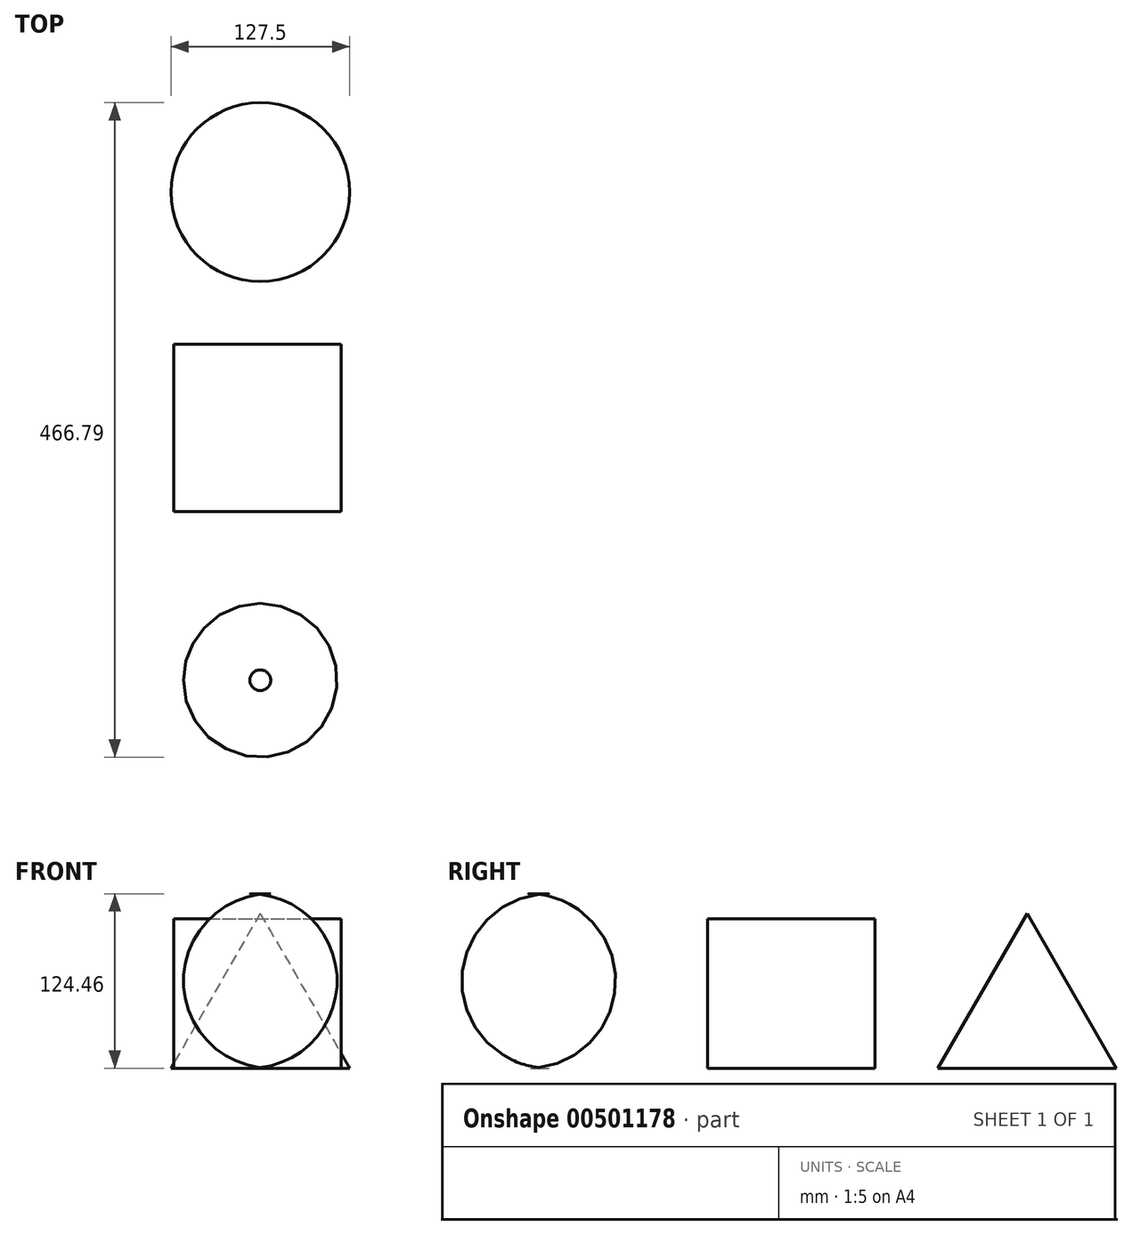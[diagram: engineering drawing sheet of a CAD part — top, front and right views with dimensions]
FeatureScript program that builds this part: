
annotation { "Feature Type Name" : "Feature", "Feature Type Description" : "" }
export const myFeature = defineFeature(function(context is Context, id is Id, definition is map)
    precondition{}
    {
        {
            var Q0;
            Q0=qCreatedBy(makeId("Top.planeOp"),FACE);
            var sketch = newSketch(context, id + "F0", { "sketchPlane" : qUnion([Q0])});
            skCircle(sketch, "E0", {"center": v(0, 0) * mm, "radius": 63.75 * mm});
            skSolve(sketch);
        }
        {
            var Q0;
            Q0=makeQuery(id+"F0.imprint","IMPRINT",FACE,{"disambiguationData":[TD([[makeQuery(id+"F0.imprint","IMPRINT",EDGE,{"derivedFrom":sQuery(id+"F0.wireOp",EDGE,"E0")}),1.0]])]});
            extrude(context, id + "F1", {"entities" : qUnion([Q0]), "depth" : 153.67 * mm, "hasDraft" : true, "draftAngle" : 30 * degree, "draftPullDirection" : true});
        }
        {
            var Q0;
            Q0=qCreatedBy(makeId("Top.planeOp"),FACE);
            var sketch = newSketch(context, id + "F2", { "sketchPlane" : qUnion([Q0])});
            skLineSegment(sketch, "E1.bottom", {"start": v(-61.61, -108.4) * mm, "end": v(57.78, -108.4) * mm});
            skLineSegment(sketch, "E1.top", {"start": v(-61.61, -227.8) * mm, "end": v(57.78, -227.8) * mm});
            skLineSegment(sketch, "E1.left", {"start": v(-61.61, -108.4) * mm, "end": v(-61.61, -227.8) * mm});
            skLineSegment(sketch, "E1.right", {"start": v(57.78, -108.4) * mm, "end": v(57.78, -227.8) * mm});
            skSolve(sketch);
        }
        {
            var Q0;
            Q0=makeQuery(id+"F2.imprint","IMPRINT",FACE,{"disambiguationData":[TD([[makeQuery(id+"F2.imprint","IMPRINT",EDGE,{"derivedFrom":sQuery(id+"F2.wireOp",EDGE,"E1.bottom")}),-1.0]])]});
            extrude(context, id + "F3", {"entities" : qUnion([Q0]), "depth" : 106.68 * mm});
        }
        {
            var Q0;
            Q0=qCreatedBy(makeId("Top.planeOp"),FACE);
            var sketch = newSketch(context, id + "F4", { "sketchPlane" : qUnion([Q0])});
            skCircle(sketch, "E2", {"center": v(0, -348.24) * mm, "radius": 69.65 * mm});
            skSolve(sketch);
        }
        {
            var Q0;
            Q0=makeQuery(id+"F4.imprint","IMPRINT",FACE,{"disambiguationData":[TD([[makeQuery(id+"F4.imprint","IMPRINT",EDGE,{"derivedFrom":sQuery(id+"F4.wireOp",EDGE,"E2")}),1.0]])]});
            extrude(context, id + "F5", {"entities" : qUnion([Q0]), "depth" : 124.46 * mm});
        }
        {
            var Q0;
            Q0=makeQuery(id+"F5.opExtrude","CAP_EDGE",EDGE,{"disambiguationData":[OSD([sQuery(id+"F4.wireOp",EDGE,"E2")])],"isStart":true});
            var Q1;
            Q1=makeQuery(id+"F5.opExtrude","CAP_EDGE",EDGE,{"disambiguationData":[OSD([sQuery(id+"F4.wireOp",EDGE,"E2")])],"isStart":false});
            fillet(context, id + "F6", {"entities" : qUnion([Q0, Q1]), "radius" : 62.23 * mm, "tangentPropagation" : true, "allowEdgeOverflow" : false});
        }
    });
